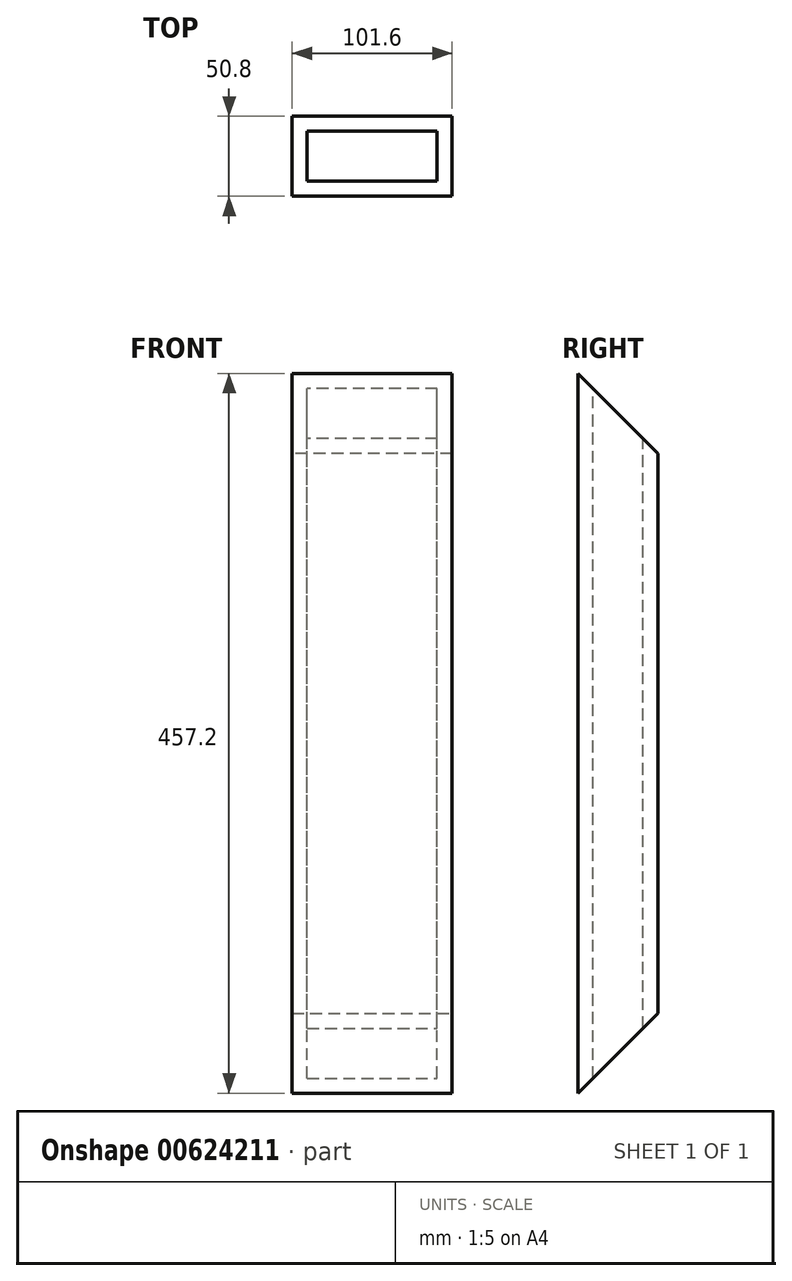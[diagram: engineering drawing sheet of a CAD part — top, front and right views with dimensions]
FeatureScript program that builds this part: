
annotation { "Feature Type Name" : "Feature", "Feature Type Description" : "" }
export const myFeature = defineFeature(function(context is Context, id is Id, definition is map)
    precondition{}
    {
        {
            var Q0;
            Q0=qCreatedBy(makeId("Top.planeOp"),FACE);
            var sketch = newSketch(context, id + "F0", { "sketchPlane" : qUnion([Q0])});
            skLineSegment(sketch, "E0.bottom", {"start": v(0, 0) * mm, "end": v(101.6, 0) * mm});
            skLineSegment(sketch, "E0.top", {"start": v(0, 50.8) * mm, "end": v(101.6, 50.8) * mm});
            skLineSegment(sketch, "E0.left", {"start": v(0, 0) * mm, "end": v(0, 50.8) * mm});
            skLineSegment(sketch, "E0.right", {"start": v(101.6, 0) * mm, "end": v(101.6, 50.8) * mm});
            skSolve(sketch);
        }
        {
            var Q0;
            Q0=makeQuery(id+"F0.imprint","IMPRINT",FACE,{"disambiguationData":[TD([[makeQuery(id+"F0.imprint","IMPRINT",EDGE,{"derivedFrom":sQuery(id+"F0.wireOp",EDGE,"E0.bottom")}),1.0]])]});
            extrude(context, id + "F1", {"entities" : qUnion([Q0]), "depth" : 457.2 * mm, "offsetDistance" : 25.4 * mm});
        }
        {
            var Q0;
            Q0=makeQuery(id+"F1.opExtrude","CAP_FACE",FACE,{"disambiguationData":[OSD([sQuery(id+"F0.wireOp",EDGE,"E0.bottom"),sQuery(id+"F0.wireOp",EDGE,"E0.top"),sQuery(id+"F0.wireOp",EDGE,"E0.left"),sQuery(id+"F0.wireOp",EDGE,"E0.right")])],"isStart":false});
            var sketch = newSketch(context, id + "F2", { "sketchPlane" : qUnion([Q0])});
            skLineSegment(sketch, "E1.bottom", {"start": v(9.52, 9.53) * mm, "end": v(92.08, 9.53) * mm});
            skLineSegment(sketch, "E1.top", {"start": v(9.52, 41.27) * mm, "end": v(92.08, 41.27) * mm});
            skLineSegment(sketch, "E1.left", {"start": v(9.52, 9.53) * mm, "end": v(9.52, 41.27) * mm});
            skLineSegment(sketch, "E1.right", {"start": v(92.08, 9.53) * mm, "end": v(92.08, 41.27) * mm});
            skSolve(sketch);
        }
        {
            var Q0;
            Q0=makeQuery(id+"F2.imprint","IMPRINT",FACE,{"disambiguationData":[TD([[makeQuery(id+"F2.imprint","IMPRINT",EDGE,{"derivedFrom":sQuery(id+"F2.wireOp",EDGE,"E1.bottom")}),1.0]])]});
            extrude(context, id + "F3", {"entities" : qUnion([Q0]), "operationType" : NewBodyOperationType.REMOVE, "oppositeDirection" : true, "depth" : 457.2 * mm, "offsetDistance" : 25.4 * mm});
        }
        {
            var Q0;
            Q0=makeQuery(id+"F1.opExtrude","SWEPT_FACE",FACE,{"disambiguationData":[OSD([sQuery(id+"F0.wireOp",EDGE,"E0.right")])]});
            var sketch = newSketch(context, id + "F4", { "sketchPlane" : qUnion([Q0])});
            skLineSegment(sketch, "E2.bottom", {"start": v(0, 0) * mm, "end": v(50.8, 0) * mm});
            skLineSegment(sketch, "E2.right", {"start": v(50.8, 0) * mm, "end": v(50.8, 50.8) * mm});
            skLineSegment(sketch, "E3", {"start": v(0, 0) * mm, "end": v(50.8, 50.8) * mm});
            skSolve(sketch);
        }
        {
            var Q0;
            Q0=makeQuery(id+"F4.imprint","IMPRINT",FACE,{"disambiguationData":[TD([[makeQuery(id+"F4.imprint","IMPRINT",EDGE,{"derivedFrom":sQuery(id+"F4.wireOp",EDGE,"E2.bottom")}),1.0]])]});
            extrude(context, id + "F5", {"entities" : qUnion([Q0]), "operationType" : NewBodyOperationType.REMOVE, "oppositeDirection" : true, "depth" : 101.6 * mm, "offsetDistance" : 25.4 * mm});
        }
        {
            var Q0;
            Q0=makeQuery(id+"F1.opExtrude","SWEPT_FACE",FACE,{"disambiguationData":[OSD([sQuery(id+"F0.wireOp",EDGE,"E0.left")])]});
            var sketch = newSketch(context, id + "F6", { "sketchPlane" : qUnion([Q0])});
            skLineSegment(sketch, "E4.bottom", {"start": v(-50.8, 457.2) * mm, "end": v(0, 457.2) * mm});
            skLineSegment(sketch, "E4.left", {"start": v(-50.8, 457.2) * mm, "end": v(-50.8, 406.4) * mm});
            skLineSegment(sketch, "E5", {"start": v(0, 457.2) * mm, "end": v(-50.8, 406.4) * mm});
            skSolve(sketch);
        }
        {
            var Q0;
            Q0 = qSketchRegion(id + "F6", true);
            extrude(context, id + "F7", {"entities" : qUnion([Q0]), "operationType" : NewBodyOperationType.REMOVE, "oppositeDirection" : true, "depth" : 101.6 * mm, "offsetDistance" : 25.4 * mm});
        }
    });
